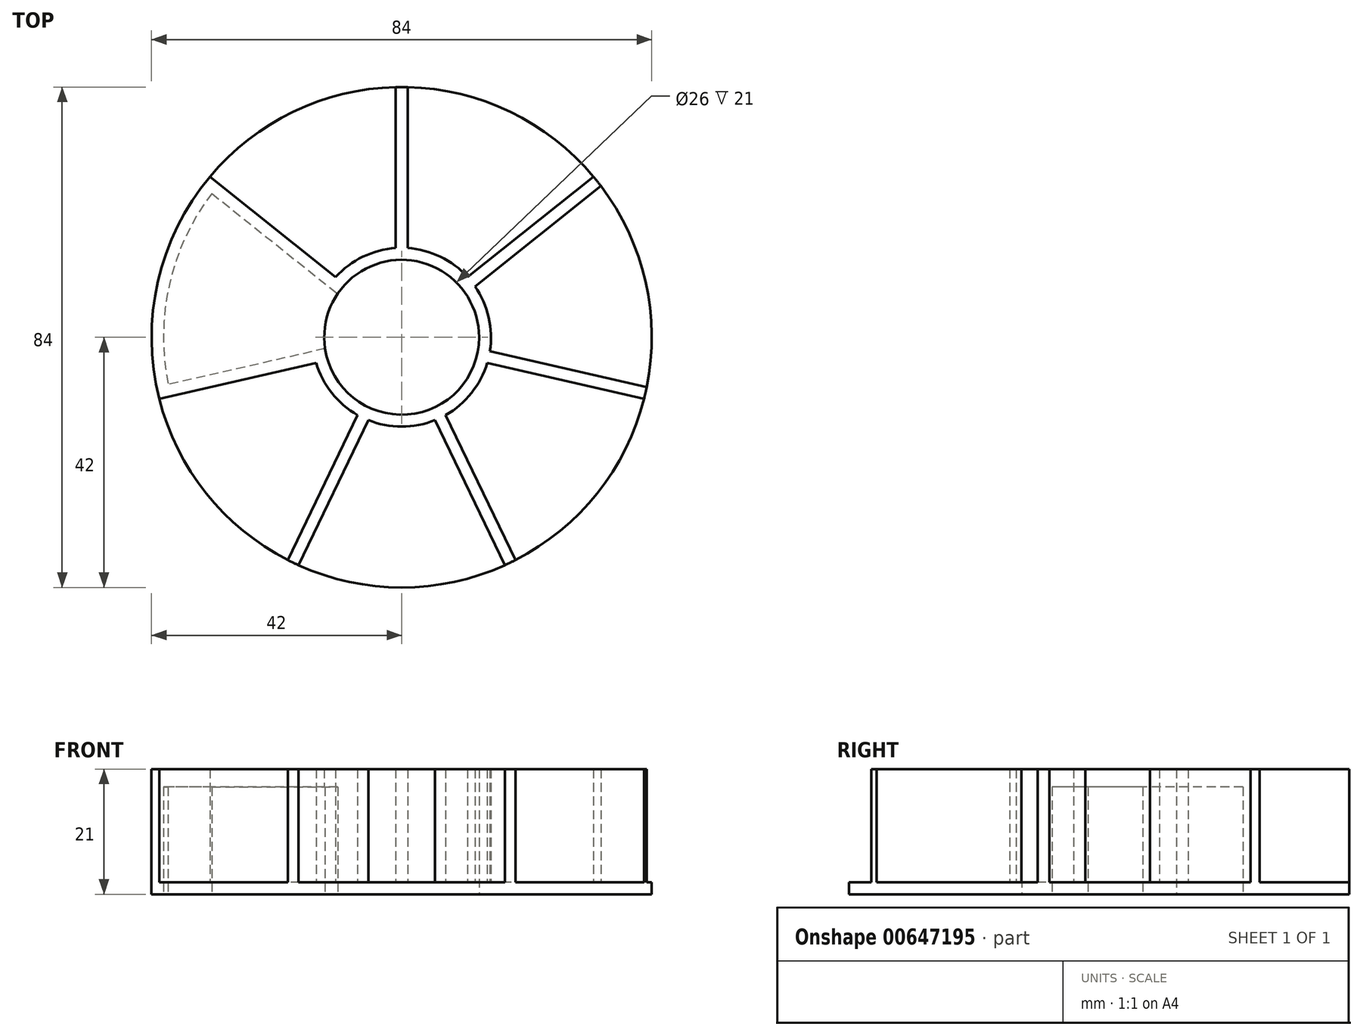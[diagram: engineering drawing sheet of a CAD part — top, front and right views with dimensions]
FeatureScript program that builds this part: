
annotation { "Feature Type Name" : "Feature", "Feature Type Description" : "" }
export const myFeature = defineFeature(function(context is Context, id is Id, definition is map)
    precondition{}
    {
        {
            var Q0;
            Q0=qCreatedBy(makeId("Top.planeOp"),FACE);
            var sketch = newSketch(context, id + "F0", { "sketchPlane" : qUnion([Q0])});
            skCircle(sketch, "E0", {"center": v(0, 0) * mm, "radius": 42 * mm});
            skCircle(sketch, "E1", {"center": v(0, 0) * mm, "radius": 13 * mm});
            skSolve(sketch);
        }
        {
            var Q0;
            Q0=qCreatedBy(makeId("Top.planeOp"),FACE);
            cPlane(context, id + "F1", {"entities" : qUnion([Q0]), "cplaneType" : CPlaneType.OFFSET, "offset" : 2 * mm, "width" : 150 * mm, "height" : 150 * mm});
        }
        {
            var Q0;
            Q0=qCreatedBy(id+"F1.planeOp",FACE);
            var sketch = newSketch(context, id + "F2", { "sketchPlane" : qUnion([Q0])});
            skLineSegment(sketch, "E2", {"start": v(1, 13.99) * mm, "end": v(1, 43.99) * mm});
            skLineSegment(sketch, "E3", {"start": v(-1, 13.99) * mm, "end": v(-1, 43.99) * mm});
            skLineSegment(sketch, "E4.1.1", {"start": v(-10.31, 9.5) * mm, "end": v(-33.77, 28.2) * mm});
            skLineSegment(sketch, "E4.2.0", {"start": v(-13.42, -4.09) * mm, "end": v(-42.66, -10.76) * mm});
            skLineSegment(sketch, "E4.3.0", {"start": v(-5.17, -13.04) * mm, "end": v(-18.18, -40.07) * mm});
            skLineSegment(sketch, "E4.3.1", {"start": v(-6.97, -12.17) * mm, "end": v(-19.99, -39.2) * mm});
            skLineSegment(sketch, "E4.4.0", {"start": v(6.97, -12.17) * mm, "end": v(19.99, -39.2) * mm});
            skLineSegment(sketch, "E4.4.1", {"start": v(5.17, -13.04) * mm, "end": v(18.18, -40.07) * mm});
            skLineSegment(sketch, "E4.5.0", {"start": v(13.86, -2.14) * mm, "end": v(43.1, -8.81) * mm});
            skLineSegment(sketch, "E4.5.1", {"start": v(13.42, -4.09) * mm, "end": v(42.66, -10.76) * mm});
            skLineSegment(sketch, "E4.6.0", {"start": v(10.31, 9.5) * mm, "end": v(33.77, 28.2) * mm});
            skLineSegment(sketch, "E4.6.1", {"start": v(11.56, 7.94) * mm, "end": v(35.02, 26.64) * mm});
            skPoint(sketch, "E4.center", {"position": v(0, 0) * mm});
            skArc(sketch, "E5", {"start": v(12.32, 8.55) * mm, "mid": v(14.62, 3.34) * mm, "end": v(14.81, -2.36) * mm});
            skArc(sketch, "E6", {"start": v(7.4, -13.05) * mm, "mid": v(11.73, -9.35) * mm, "end": v(14.37, -4.3) * mm});
            skArc(sketch, "E7", {"start": v(-5.6, -13.92) * mm, "mid": v(0, -15) * mm, "end": v(5.6, -13.92) * mm});
            skArc(sketch, "E8", {"start": v(-14.37, -4.3) * mm, "mid": v(-11.73, -9.35) * mm, "end": v(-7.4, -13.05) * mm});
            skArc(sketch, "E9", {"start": v(-1, 14.97) * mm, "mid": v(-6.5, 13.51) * mm, "end": v(-11.08, 10.11) * mm});
            skArc(sketch, "E10", {"start": v(1, 14.97) * mm, "mid": v(6.5, 13.51) * mm, "end": v(11.08, 10.11) * mm});
            skArc(sketch, "E11", {"start": v(1, 43.99) * mm, "mid": v(19.1, 39.64) * mm, "end": v(33.77, 28.2) * mm});
            skArc(sketch, "E12", {"start": v(35.02, 26.64) * mm, "mid": v(42.9, 9.8) * mm, "end": v(43.1, -8.81) * mm});
            skArc(sketch, "E13", {"start": v(42.66, -10.76) * mm, "mid": v(34.4, -27.43) * mm, "end": v(19.99, -39.2) * mm});
            skArc(sketch, "E14", {"start": v(18.18, -40.07) * mm, "mid": v(0, -44) * mm, "end": v(-18.18, -40.07) * mm});
            skArc(sketch, "E15", {"start": v(-19.99, -39.2) * mm, "mid": v(-34.4, -27.43) * mm, "end": v(-42.66, -10.76) * mm});
            skArc(sketch, "E16", {"start": v(-33.77, 28.2) * mm, "mid": v(-19.1, 39.64) * mm, "end": v(-1, 43.99) * mm});
            skSolve(sketch);
        }
        {
            var Q0;
            Q0 = qSketchRegion(id + "F0", true);
            var Q1;
            Q1=makeQuery(id+"F0.imprint","IMPRINT",FACE,{"disambiguationData":[TD([[makeQuery(id+"F0.imprint","IMPRINT",EDGE,{"derivedFrom":sQuery(id+"F0.wireOp",EDGE,"i4FpL0Lj-bHaC-CIhp-7WTi-7HsbGognGMwQ")}),1.0]])]});
            extrude(context, id + "F3", {"entities" : qUnion([Q0, Q1]), "depth" : 21 * mm, "offsetDistance" : 25 * mm});
        }
        {
            var Q0;
            Q0 = qSketchRegion(id + "F2", true);
            extrude(context, id + "F4", {"entities" : qUnion([Q0]), "operationType" : NewBodyOperationType.REMOVE, "depth" : 25 * mm, "offsetDistance" : 25 * mm});
        }
        {
            var Q0;
            Q0=makeQuery(id+"F4.boolean.opBoolean","COPY",FACE,{"derivedFrom":makeQuery(id+"F4.opExtrude","SWEPT_FACE",FACE,{"disambiguationData":[OSD([sQuery(id+"F2.wireOp",EDGE,"E4.1.1")])]})});
            cPlane(context, id + "F5", {"entities" : qUnion([Q0]), "cplaneType" : CPlaneType.OFFSET, "offset" : 0 * mm, "oppositeDirection" : true, "width" : 150 * mm, "height" : 150 * mm});
        }
        {
            var Q0;
            Q0=makeQuery(id+"F4.boolean.opBoolean","COPY",FACE,{"derivedFrom":makeQuery(id+"F4.opExtrude","SWEPT_FACE",FACE,{"disambiguationData":[OSD([sQuery(id+"F2.wireOp",EDGE,"E4.2.0")])]})});
            cPlane(context, id + "F6", {"entities" : qUnion([Q0]), "cplaneType" : CPlaneType.OFFSET, "offset" : 0 * mm, "width" : 150 * mm, "height" : 150 * mm});
        }
        {
            var Q0;
            Q0=makeQuery(id+"F0.imprint","IMPRINT",FACE,{"disambiguationData":[TD([[makeQuery(id+"F0.imprint","IMPRINT",EDGE,{"derivedFrom":sQuery(id+"F0.wireOp",EDGE,"E0")}),1.0]])]});
            cPlane(context, id + "F7", {"entities" : qUnion([Q0]), "cplaneType" : CPlaneType.OFFSET, "offset" : 0 * mm, "width" : 150 * mm, "height" : 150 * mm});
        }
        {
            var Q0;
            Q0=qCreatedBy(id+"F7.planeOp",FACE);
            var sketch = newSketch(context, id + "F8", { "sketchPlane" : qUnion([Q0])});
            skLineSegment(sketch, "E17", {"start": v(-40.71, -10.32) * mm, "end": v(-12.41, -3.86) * mm});
            skLineSegment(sketch, "E18", {"start": v(-32.2, 26.96) * mm, "end": v(-9.51, 8.86) * mm});
            skLineSegment(sketch, "E19", {"start": v(-12.86, -1.9) * mm, "end": v(-41.16, -8.37) * mm});
            skLineSegment(sketch, "E20", {"start": v(-33.45, 25.4) * mm, "end": v(-10.76, 7.3) * mm});
            skArc(sketch, "E21", {"start": v(-31.89, 24.15) * mm, "mid": v(-39, 8.9) * mm, "end": v(-39.2, -7.92) * mm});
            skArc(sketch, "E22", {"start": v(-10.76, 7.3) * mm, "mid": v(-12.67, 2.9) * mm, "end": v(-12.86, -1.9) * mm});
            skSolve(sketch);
        }
        {
            var Q0;
            {var subQ0=sQuery(id+"F8.wireOp",EDGE,"E21");Q0=makeQuery(id+"F8.imprint","IMPRINT",FACE,{"disambiguationData":[TD([[makeQuery(id+"F8.imprint","IMPRINT",EDGE,{"derivedFrom":subQ0}),1.0]])]});}
            extrude(context, id + "F9", {"entities" : qUnion([Q0]), "operationType" : NewBodyOperationType.REMOVE, "depth" : 18 * mm, "offsetDistance" : 25 * mm});
        }
    });
